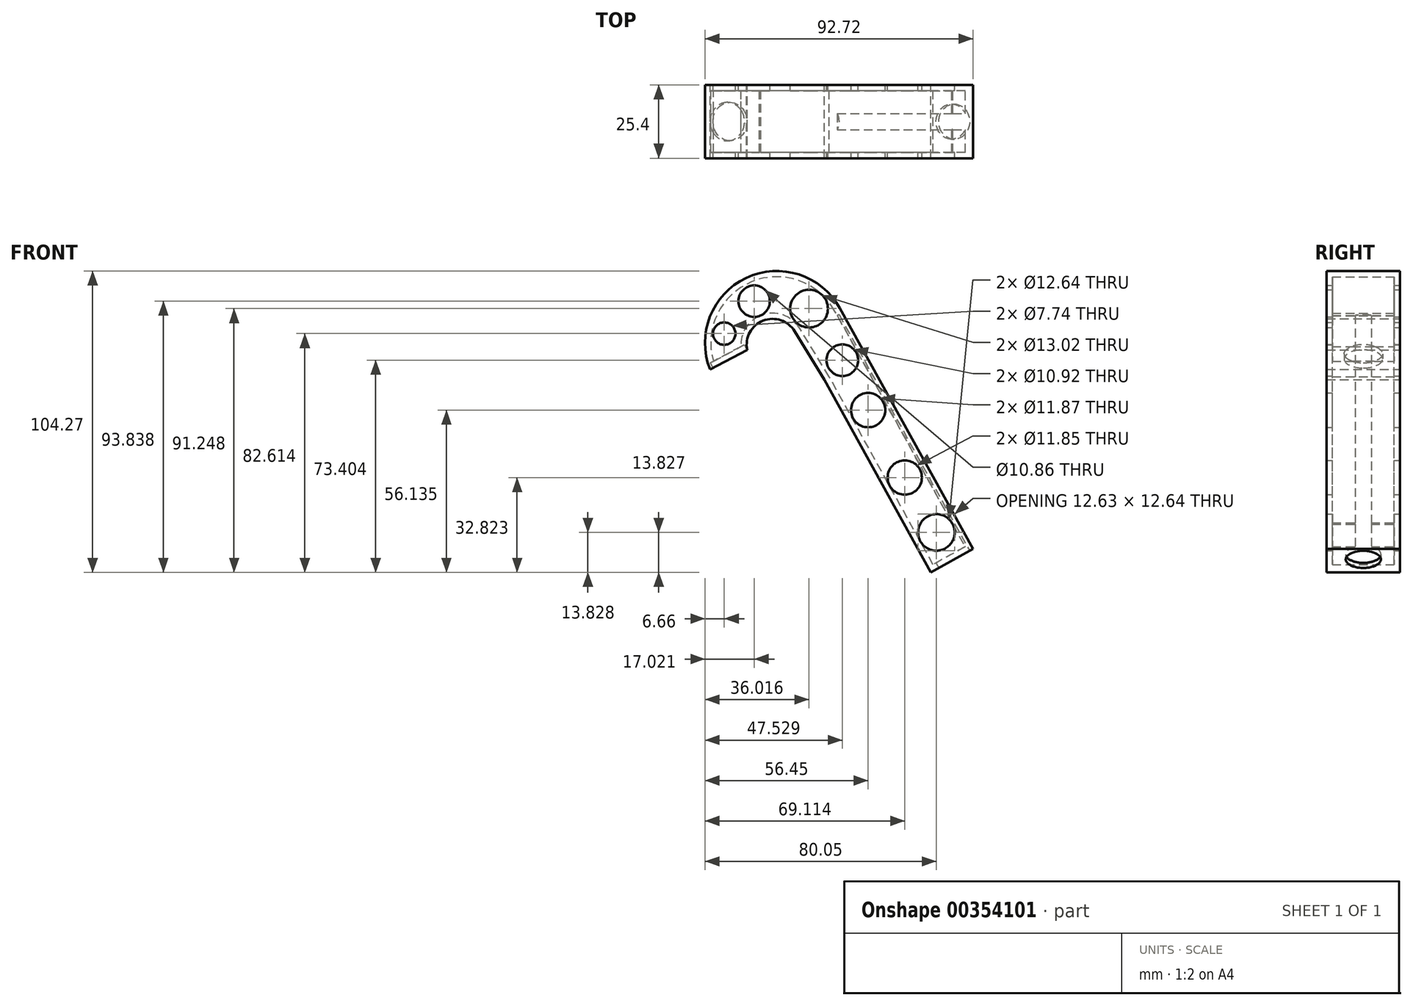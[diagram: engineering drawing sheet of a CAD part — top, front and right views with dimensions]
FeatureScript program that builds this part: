
annotation { "Feature Type Name" : "Feature", "Feature Type Description" : "" }
export const myFeature = defineFeature(function(context is Context, id is Id, definition is map)
    precondition{}
    {
        {
            var Q0;
            Q0=qCreatedBy(makeId("Front.planeOp"),FACE);
            var sketch = newSketch(context, id + "F0", { "sketchPlane" : qUnion([Q0])});
            skLineSegment(sketch, "E0", {"start": v(29.65, -38.27) * mm, "end": v(-16.43, 45.08) * mm});
            skLineSegment(sketch, "E1", {"start": v(29.65, -38.27) * mm, "end": v(15.04, -46.35) * mm});
            skLineSegment(sketch, "E2", {"start": v(15.04, -46.35) * mm, "end": v(-21.82, 20.32) * mm});
            skArc(sketch, "E3", {"start": v(-16.43, 45.08) * mm, "mid": v(-48.84, 55.53) * mm, "end": v(-61.3, 23.84) * mm});
            skLineSegment(sketch, "E4", {"start": v(-21.82, 20.32) * mm, "end": v(-32.06, 37.06) * mm});
            skLineSegment(sketch, "E5", {"start": v(-61.3, 23.84) * mm, "end": v(-48.48, 30.65) * mm});
            skArc(sketch, "E6", {"start": v(-32.06, 37.06) * mm, "mid": v(-42.95, 40.74) * mm, "end": v(-48.48, 30.65) * mm});
            skSolve(sketch);
        }
        {
            var Q0;
            Q0 = qSketchRegion(id + "F0", true);
            extrude(context, id + "F1", {"entities" : qUnion([Q0]), "depth" : 25.4 * mm});
        }
        {
            var Q0;
            Q0=qCreatedBy(makeId("Front.planeOp"),FACE);
            var sketch = newSketch(context, id + "F2", { "sketchPlane" : qUnion([Q0])});
            skCircle(sketch, "E7", {"center": v(16.98, -32.52) * mm, "radius": 6.32 * mm});
            skCircle(sketch, "E8", {"center": v(6.04, -13.53) * mm, "radius": 5.93 * mm});
            skCircle(sketch, "E9", {"center": v(-6.62, 9.79) * mm, "radius": 5.93 * mm});
            skCircle(sketch, "E10", {"center": v(-15.54, 27.05) * mm, "radius": 5.46 * mm});
            skCircle(sketch, "E11", {"center": v(-27.05, 44.9) * mm, "radius": 6.51 * mm});
            skCircle(sketch, "E12", {"center": v(-56.4, 36.26) * mm, "radius": 3.87 * mm});
            skCircle(sketch, "E13", {"center": v(-46.05, 47.49) * mm, "radius": 5.43 * mm});
            skSolve(sketch);
        }
        {
            var Q0;
            Q0=makeQuery(id+"F8.boolean.opBoolean","COPY",FACE,{"derivedFrom":makeQuery(id+"F8.opExtrude","SWEPT_FACE",FACE,{"disambiguationData":[OSD([sQuery(id+"F7.wireOp",EDGE,"E15")])]})});
            var Q1;
            Q1=makeQuery(id+"F1.opExtrude","SWEPT_BODY",BODY,{"disambiguationData":[OSD([sQuery(id+"F0.wireOp",EDGE,"E0"),sQuery(id+"F0.wireOp",EDGE,"E1"),sQuery(id+"F0.wireOp",EDGE,"E2"),sQuery(id+"F0.wireOp",EDGE,"E3"),sQuery(id+"F0.wireOp",EDGE,"E4"),sQuery(id+"F0.wireOp",EDGE,"E5"),sQuery(id+"F0.wireOp",EDGE,"E6")])]});
            shell(context, id + "F3", {"isHollow" : true, "entities" : qUnion([Q0]), "parts" : qUnion([Q1]), "thickness" : 2 * mm});
        }
        {
            var Q0;
            Q0 = qSketchRegion(id + "F2", true);
            extrude(context, id + "F4", {"entities" : qUnion([Q0]), "operationType" : NewBodyOperationType.REMOVE, "depth" : 25.4 * mm});
        }
        {
            var Q0;
            Q0=makeQuery(id+"F1.opExtrude","SWEPT_FACE",FACE,{"disambiguationData":[OSD([sQuery(id+"F0.wireOp",EDGE,"E1")])]});
            var sketch = newSketch(context, id + "F5", { "sketchPlane" : qUnion([Q0])});
            skCircle(sketch, "E14", {"center": v(0, 12.7) * mm, "radius": 6.1 * mm});
            skPoint(sketch, "E14.centerSnap0", {"position": v(7.43, 12.7) * mm});
            skSolve(sketch);
        }
        {
            var Q0;
            Q0=makeQuery(id+"F5.imprint","IMPRINT",FACE,{"disambiguationData":[TD([[makeQuery(id+"F5.imprint","IMPRINT",EDGE,{"derivedFrom":sQuery(id+"F5.wireOp",EDGE,"E14")}),1.0]])]});
            extrude(context, id + "F6", {"entities" : qUnion([Q0]), "operationType" : NewBodyOperationType.REMOVE, "oppositeDirection" : true, "depth" : 93.47 * mm});
        }
        {
            var Q0;
            Q0=makeQuery(id+"F1.opExtrude","SWEPT_FACE",FACE,{"disambiguationData":[OSD([sQuery(id+"F0.wireOp",EDGE,"E5")])]});
            var sketch = newSketch(context, id + "F7", { "sketchPlane" : qUnion([Q0])});
            skCircle(sketch, "E15", {"center": v(-35.16, 12.7) * mm, "radius": 6.66 * mm});
            skPoint(sketch, "E15.centerSnap0", {"position": v(-28.44, 12.7) * mm});
            skSolve(sketch);
        }
        {
            var Q0;
            Q0=makeQuery(id+"F7.imprint","IMPRINT",FACE,{"disambiguationData":[TD([[makeQuery(id+"F7.imprint","IMPRINT",EDGE,{"derivedFrom":sQuery(id+"F7.wireOp",EDGE,"E15")}),1.0]])]});
            extrude(context, id + "F8", {"entities" : qUnion([Q0]), "operationType" : NewBodyOperationType.REMOVE, "oppositeDirection" : true, "depth" : 2.03 * mm});
        }
    });
